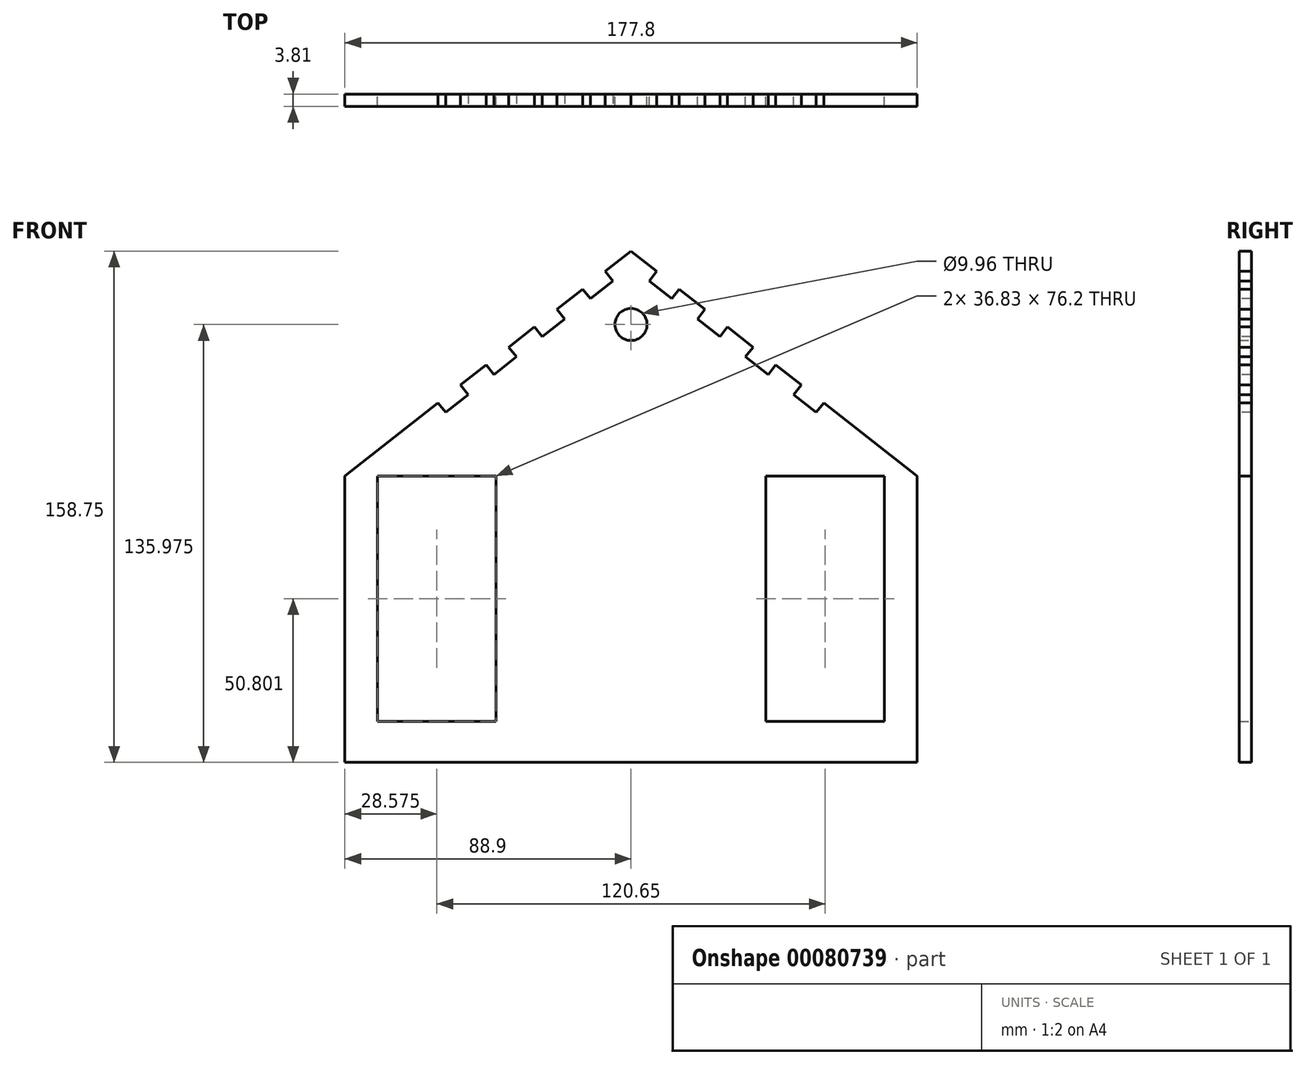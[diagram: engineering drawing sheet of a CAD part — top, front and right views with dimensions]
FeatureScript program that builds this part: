
annotation { "Feature Type Name" : "Feature", "Feature Type Description" : "" }
export const myFeature = defineFeature(function(context is Context, id is Id, definition is map)
    precondition{}
    {
        {
            var Q0;
            Q0=qCreatedBy(makeId("Front.planeOp"),FACE);
            var sketch = newSketch(context, id + "F0", { "sketchPlane" : qUnion([Q0])});
            skLineSegment(sketch, "E0", {"start": v(0, 92.74) * mm, "end": v(0, -66) * mm, "construction": true});
            skLineSegment(sketch, "E1", {"start": v(0, -66) * mm, "end": v(-88.9, -66) * mm});
            skLineSegment(sketch, "E2.MirrorCS", {"start": v(0, -66) * mm, "end": v(88.9, -66) * mm});
            skLineSegment(sketch, "E3", {"start": v(-88.9, -66) * mm, "end": v(-88.9, 22.9) * mm});
            skLineSegment(sketch, "E4", {"start": v(-88.9, 22.9) * mm, "end": v(0, 92.74) * mm});
            skLineSegment(sketch, "E5.MirrorCS", {"start": v(88.9, -66) * mm, "end": v(88.9, 22.9) * mm});
            skLineSegment(sketch, "E6.MirrorCS", {"start": v(88.9, 22.9) * mm, "end": v(0, 92.74) * mm});
            skLineSegment(sketch, "E7.bottom", {"start": v(-78.74, 22.9) * mm, "end": v(-41.91, 22.9) * mm});
            skLineSegment(sketch, "E7.top", {"start": v(-78.74, -53.3) * mm, "end": v(-41.9, -53.3) * mm});
            skLineSegment(sketch, "E7.left", {"start": v(-78.74, 22.9) * mm, "end": v(-78.74, -53.3) * mm});
            skLineSegment(sketch, "E7.right", {"start": v(-41.9, 22.9) * mm, "end": v(-41.9, -53.3) * mm});
            skPoint(sketch, "E7.middle", {"position": v(-60.32, -15.2) * mm});
            skLineSegment(sketch, "E8.MirrorCS", {"start": v(41.91, 22.9) * mm, "end": v(41.91, -53.3) * mm});
            skLineSegment(sketch, "E9.MirrorCS", {"start": v(78.74, 22.9) * mm, "end": v(41.91, 22.9) * mm});
            skLineSegment(sketch, "E10.MirrorCS", {"start": v(78.74, 22.9) * mm, "end": v(78.74, -53.3) * mm});
            skLineSegment(sketch, "E11.MirrorCS", {"start": v(78.74, -53.3) * mm, "end": v(41.91, -53.3) * mm});
            skSolve(sketch);
        }
        {
            var Q0;
            Q0=makeQuery(id+"F0.imprint","IMPRINT",FACE,{"disambiguationData":[TD([[makeQuery(id+"F0.imprint","IMPRINT",EDGE,{"derivedFrom":sQuery(id+"F0.wireOp",EDGE,"E1")}),-1.0]])]});
            extrude(context, id + "F1", {"entities" : qUnion([Q0]), "depth" : 3.8 * mm});
        }
        {
            var Q0;
            Q0=makeQuery(id+"F1.opExtrude","SWEPT_FACE",FACE,{"disambiguationData":[OSD([sQuery(id+"F0.wireOp",EDGE,"E4")])]});
            var sketch = newSketch(context, id + "F2", { "sketchPlane" : qUnion([Q0])});
            skLineSegment(sketch, "E12.bottom", {"start": v(-18.9, 0) * mm, "end": v(-10.01, 0) * mm});
            skLineSegment(sketch, "E12.top", {"start": v(-18.9, -3.81) * mm, "end": v(-10.01, -3.81) * mm});
            skLineSegment(sketch, "E12.left", {"start": v(-18.9, 0) * mm, "end": v(-18.9, -3.81) * mm});
            skLineSegment(sketch, "E12.right", {"start": v(-10.01, 0) * mm, "end": v(-10.01, -3.81) * mm});
            skLineSegment(sketch, "E13.bottom", {"start": v(0.15, 0) * mm, "end": v(9.04, 0) * mm});
            skLineSegment(sketch, "E13.top", {"start": v(0.15, -3.81) * mm, "end": v(9.04, -3.81) * mm});
            skLineSegment(sketch, "E13.left", {"start": v(0.15, 0) * mm, "end": v(0.15, -3.81) * mm});
            skLineSegment(sketch, "E13.right", {"start": v(9.04, 0) * mm, "end": v(9.04, -3.81) * mm});
            skLineSegment(sketch, "E14.bottom", {"start": v(19.2, 0) * mm, "end": v(28.09, 0) * mm});
            skLineSegment(sketch, "E14.top", {"start": v(19.2, -3.81) * mm, "end": v(28.09, -3.81) * mm});
            skLineSegment(sketch, "E14.left", {"start": v(19.2, 0) * mm, "end": v(19.2, -3.81) * mm});
            skLineSegment(sketch, "E14.right", {"start": v(28.09, 0) * mm, "end": v(28.09, -3.81) * mm});
            skLineSegment(sketch, "E15.bottom", {"start": v(38.25, 0) * mm, "end": v(47.14, 0) * mm});
            skLineSegment(sketch, "E15.top", {"start": v(38.25, -3.81) * mm, "end": v(47.14, -3.81) * mm});
            skLineSegment(sketch, "E15.left", {"start": v(38.25, 0) * mm, "end": v(38.25, -3.81) * mm});
            skLineSegment(sketch, "E15.right", {"start": v(47.14, 0) * mm, "end": v(47.14, -3.81) * mm});
            skSolve(sketch);
        }
        {
            var Q0;
            Q0=makeQuery(id+"F2.imprint","IMPRINT",FACE,{"disambiguationData":[TD([[makeQuery(id+"F2.imprint","IMPRINT",EDGE,{"derivedFrom":sQuery(id+"F2.wireOp",EDGE,"E12.bottom")}),-1.0]])]});
            var Q1;
            Q1=makeQuery(id+"F2.imprint","IMPRINT",FACE,{"disambiguationData":[TD([[makeQuery(id+"F2.imprint","IMPRINT",EDGE,{"derivedFrom":sQuery(id+"F2.wireOp",EDGE,"E14.bottom")}),-1.0]])]});
            var Q2;
            Q2=makeQuery(id+"F2.imprint","IMPRINT",FACE,{"disambiguationData":[TD([[makeQuery(id+"F2.imprint","IMPRINT",EDGE,{"derivedFrom":sQuery(id+"F2.wireOp",EDGE,"E15.bottom")}),-1.0]])]});
            var Q3;
            Q3=makeQuery(id+"F2.imprint","IMPRINT",FACE,{"disambiguationData":[TD([[makeQuery(id+"F2.imprint","IMPRINT",EDGE,{"derivedFrom":sQuery(id+"F2.wireOp",EDGE,"E13.bottom")}),-1.0]])]});
            extrude(context, id + "F3", {"entities" : qUnion([Q0, Q1, Q2, Q3]), "operationType" : NewBodyOperationType.REMOVE, "oppositeDirection" : true, "depth" : 3.8 * mm});
        }
        {
            var Q0;
            Q0=makeQuery(id+"F1.opExtrude","SWEPT_FACE",FACE,{"disambiguationData":[OSD([sQuery(id+"F0.wireOp",EDGE,"E6.MirrorCS")])]});
            var sketch = newSketch(context, id + "F4", { "sketchPlane" : qUnion([Q0])});
            skLineSegment(sketch, "E16.bottom", {"start": v(-47.14, -3.81) * mm, "end": v(-38.25, -3.81) * mm});
            skLineSegment(sketch, "E16.top", {"start": v(-47.14, 0) * mm, "end": v(-38.25, 0) * mm});
            skLineSegment(sketch, "E16.left", {"start": v(-47.14, -3.81) * mm, "end": v(-47.14, 0) * mm});
            skLineSegment(sketch, "E16.right", {"start": v(-38.25, -3.8) * mm, "end": v(-38.25, 0) * mm});
            skLineSegment(sketch, "E17.bottom", {"start": v(-28.09, -3.81) * mm, "end": v(-19.2, -3.81) * mm});
            skLineSegment(sketch, "E17.top", {"start": v(-28.09, 0) * mm, "end": v(-19.2, 0) * mm});
            skLineSegment(sketch, "E17.left", {"start": v(-28.09, -3.81) * mm, "end": v(-28.09, 0) * mm});
            skLineSegment(sketch, "E17.right", {"start": v(-19.2, -3.81) * mm, "end": v(-19.2, 0) * mm});
            skLineSegment(sketch, "E18.bottom", {"start": v(-9.04, -3.81) * mm, "end": v(-0.15, -3.81) * mm});
            skLineSegment(sketch, "E18.top", {"start": v(-9.04, 0) * mm, "end": v(-0.15, 0) * mm});
            skLineSegment(sketch, "E18.left", {"start": v(-9.04, -3.81) * mm, "end": v(-9.04, 0) * mm});
            skLineSegment(sketch, "E18.right", {"start": v(-0.15, -3.81) * mm, "end": v(-0.15, 0) * mm});
            skLineSegment(sketch, "E19.bottom", {"start": v(10.01, -3.81) * mm, "end": v(18.9, -3.81) * mm});
            skLineSegment(sketch, "E19.top", {"start": v(10.01, 0) * mm, "end": v(18.9, 0) * mm});
            skLineSegment(sketch, "E19.left", {"start": v(10.01, -3.81) * mm, "end": v(10.01, 0) * mm});
            skLineSegment(sketch, "E19.right", {"start": v(18.9, -3.81) * mm, "end": v(18.9, 0) * mm});
            skSolve(sketch);
        }
        {
            var Q0;
            Q0=makeQuery(id+"F4.imprint","IMPRINT",FACE,{"disambiguationData":[TD([[makeQuery(id+"F4.imprint","IMPRINT",EDGE,{"derivedFrom":sQuery(id+"F4.wireOp",EDGE,"E16.bottom")}),-1.0]])]});
            var Q1;
            Q1=makeQuery(id+"F4.imprint","IMPRINT",FACE,{"disambiguationData":[TD([[makeQuery(id+"F4.imprint","IMPRINT",EDGE,{"derivedFrom":sQuery(id+"F4.wireOp",EDGE,"E17.bottom")}),-1.0]])]});
            var Q2;
            Q2=makeQuery(id+"F4.imprint","IMPRINT",FACE,{"disambiguationData":[TD([[makeQuery(id+"F4.imprint","IMPRINT",EDGE,{"derivedFrom":sQuery(id+"F4.wireOp",EDGE,"E18.bottom")}),-1.0]])]});
            var Q3;
            Q3=makeQuery(id+"F4.imprint","IMPRINT",FACE,{"disambiguationData":[TD([[makeQuery(id+"F4.imprint","IMPRINT",EDGE,{"derivedFrom":sQuery(id+"F4.wireOp",EDGE,"E19.bottom")}),-1.0]])]});
            extrude(context, id + "F5", {"entities" : qUnion([Q0, Q1, Q2, Q3]), "operationType" : NewBodyOperationType.REMOVE, "oppositeDirection" : true, "depth" : 3.8 * mm});
        }
        {
            var Q0;
            Q0=makeQuery(id+"F1.opExtrude","CAP_FACE",FACE,{"disambiguationData":[OSD([sQuery(id+"F0.wireOp",EDGE,"E1"),sQuery(id+"F0.wireOp",EDGE,"E2.MirrorCS"),sQuery(id+"F0.wireOp",EDGE,"E3"),sQuery(id+"F0.wireOp",EDGE,"E4"),sQuery(id+"F0.wireOp",EDGE,"E5.MirrorCS"),sQuery(id+"F0.wireOp",EDGE,"E6.MirrorCS"),sQuery(id+"F0.wireOp",EDGE,"E7.bottom"),sQuery(id+"F0.wireOp",EDGE,"E7.top"),sQuery(id+"F0.wireOp",EDGE,"E7.left"),sQuery(id+"F0.wireOp",EDGE,"E7.right"),sQuery(id+"F0.wireOp",EDGE,"E8.MirrorCS"),sQuery(id+"F0.wireOp",EDGE,"E9.MirrorCS"),sQuery(id+"F0.wireOp",EDGE,"E10.MirrorCS"),sQuery(id+"F0.wireOp",EDGE,"E11.MirrorCS")])],"isStart":true});
            var sketch = newSketch(context, id + "F6", { "sketchPlane" : qUnion([Q0])});
            skCircle(sketch, "E20", {"center": v(0, 69.96) * mm, "radius": 4.98 * mm});
            skSolve(sketch);
        }
        {
            var Q0;
            Q0=makeQuery(id+"F6.imprint","IMPRINT",FACE,{"disambiguationData":[TD([[makeQuery(id+"F6.imprint","IMPRINT",EDGE,{"derivedFrom":sQuery(id+"F6.wireOp",EDGE,"E20")}),1.0]])]});
            extrude(context, id + "F7", {"entities" : qUnion([Q0]), "operationType" : NewBodyOperationType.REMOVE, "oppositeDirection" : true, "depth" : 3.8 * mm});
        }
    });
